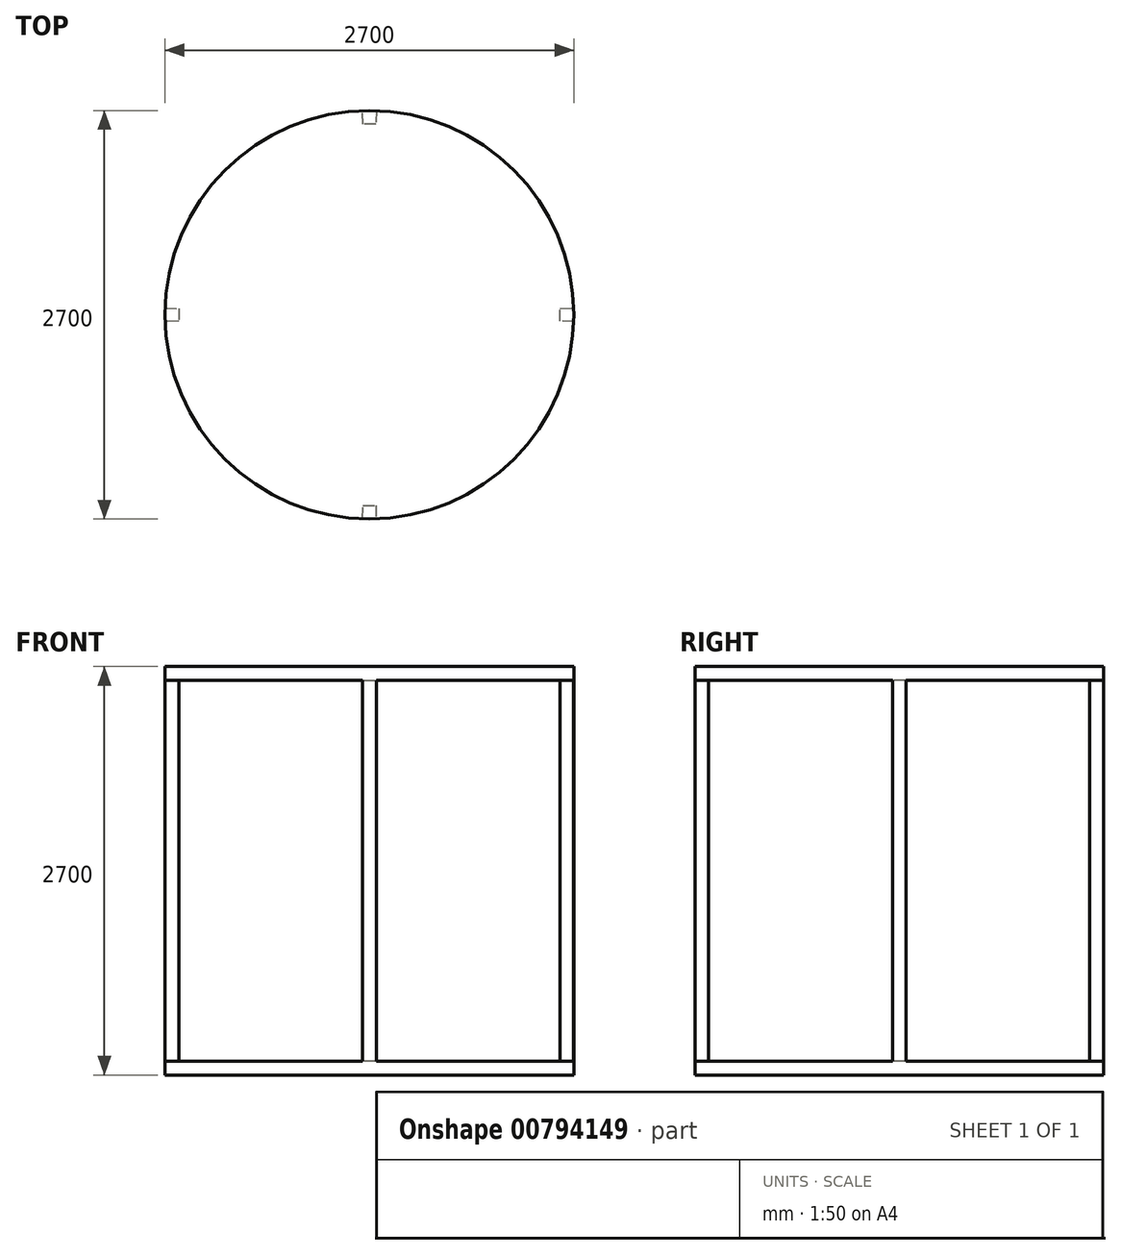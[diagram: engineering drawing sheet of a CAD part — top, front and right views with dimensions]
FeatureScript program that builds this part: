
annotation { "Feature Type Name" : "Feature", "Feature Type Description" : "" }
export const myFeature = defineFeature(function(context is Context, id is Id, definition is map)
    precondition{}
    {
        {
            var Q0;
            Q0=qCreatedBy(makeId("Top.planeOp"),FACE);
            var sketch = newSketch(context, id + "F0", { "sketchPlane" : qUnion([Q0])});
            skCircle(sketch, "E0", {"center": v(0, 0) * mm, "radius": 1350 * mm});
            skSolve(sketch);
        }
        {
            var Q0;
            Q0 = qSketchRegion(id + "F0", true);
            extrude(context, id + "F1", {"entities" : qUnion([Q0]), "depth" : 90 * mm, "offsetDistance" : 25 * mm});
        }
        {
            var Q0;
            Q0=makeQuery(id+"F1.opExtrude","CAP_FACE",FACE,{"disambiguationData":[OSD([sQuery(id+"F0.wireOp",EDGE,"E0")])],"isStart":false});
            var sketch = newSketch(context, id + "F2", { "sketchPlane" : qUnion([Q0])});
            skLineSegment(sketch, "E1", {"start": v(0, 0) * mm, "end": v(-1350, 0) * mm, "construction": true});
            skLineSegment(sketch, "E2", {"start": v(0, 0) * mm, "end": v(-1349.25, 45) * mm, "construction": true});
            skLineSegment(sketch, "E3", {"start": v(0, 0) * mm, "end": v(-1349.25, -45) * mm, "construction": true});
            skArc(sketch, "E4", {"start": v(-1349.25, 45) * mm, "mid": v(-1350, 0) * mm, "end": v(-1349.25, -45) * mm});
            skLineSegment(sketch, "E5", {"start": v(-1349.25, 45) * mm, "end": v(-1349.25, -45) * mm, "construction": true});
            skLineSegment(sketch, "E6", {"start": v(-1349.25, 45) * mm, "end": v(-1259.25, 42) * mm});
            skLineSegment(sketch, "E7", {"start": v(-1259.25, 42) * mm, "end": v(-1259.25, 0) * mm});
            skLineSegment(sketch, "E8", {"start": v(-1259.25, 0) * mm, "end": v(-1259.25, -42) * mm});
            skLineSegment(sketch, "E9", {"start": v(-1259.25, -42) * mm, "end": v(-1349.25, -45) * mm});
            skSolve(sketch);
        }
        {
            var Q0;
            Q0 = qSketchRegion(id + "F2", true);
            extrude(context, id + "F3", {"entities" : qUnion([Q0]), "operationType" : NewBodyOperationType.ADD, "depth" : (2700 - 90) * mm, "offsetDistance" : 25 * mm});
        }
        {
            var Q0;
            Q0=qCreatedBy(makeId("Right.planeOp"),FACE);
            var sketch = newSketch(context, id + "F4", { "sketchPlane" : qUnion([Q0])});
            skLineSegment(sketch, "E10", {"start": v(0, 0) * mm, "end": v(0, 795.75) * mm, "construction": true});
            skSolve(sketch);
        }
        {
            var Q0;
            Q0=makeQuery(id+"F1.opExtrude","SWEPT_BODY",BODY,{"disambiguationData":[OSD([sQuery(id+"F0.wireOp",EDGE,"E0")])]});
            var Q1;
            Q1=sQuery(id+"F4.wireOp",EDGE,"E10");
            circularPattern(context, id + "F5", {"entities" : qUnion([Q0]), "axis" : qUnion([Q1]), "angle" : 360 * degree, "instanceCount" : 4, "equalSpace" : true});
        }
        {
            var Q0;
            Q0=makeQuery(id+"F5.opPattern","COPY",FACE,{"derivedFrom":makeQuery(id+"F3.opExtrude","CAP_FACE",FACE,{"disambiguationData":[OSD([sQuery(id+"F2.wireOp",EDGE,"E4"),sQuery(id+"F2.wireOp",EDGE,"E6"),sQuery(id+"F2.wireOp",EDGE,"E7"),sQuery(id+"F2.wireOp",EDGE,"E8"),sQuery(id+"F2.wireOp",EDGE,"E9")])],"isStart":false}),"instanceName":"2"});
            var sketch = newSketch(context, id + "F6", { "sketchPlane" : qUnion([Q0])});
            skArc(sketch, "E11.0", {"start": v(-1349.25, -45) * mm, "mid": v(1350, 0) * mm, "end": v(-1349.25, 45) * mm});
            skArc(sketch, "E12", {"start": v(-1349.25, 45) * mm, "mid": v(-1350, 0) * mm, "end": v(-1349.25, -45) * mm});
            skSolve(sketch);
        }
        {
            var Q0;
            Q0 = qSketchRegion(id + "F6", true);
            extrude(context, id + "F7", {"entities" : qUnion([Q0]), "operationType" : NewBodyOperationType.ADD, "oppositeDirection" : true, "depth" : 90 * mm, "offsetDistance" : 25 * mm});
        }
    });
